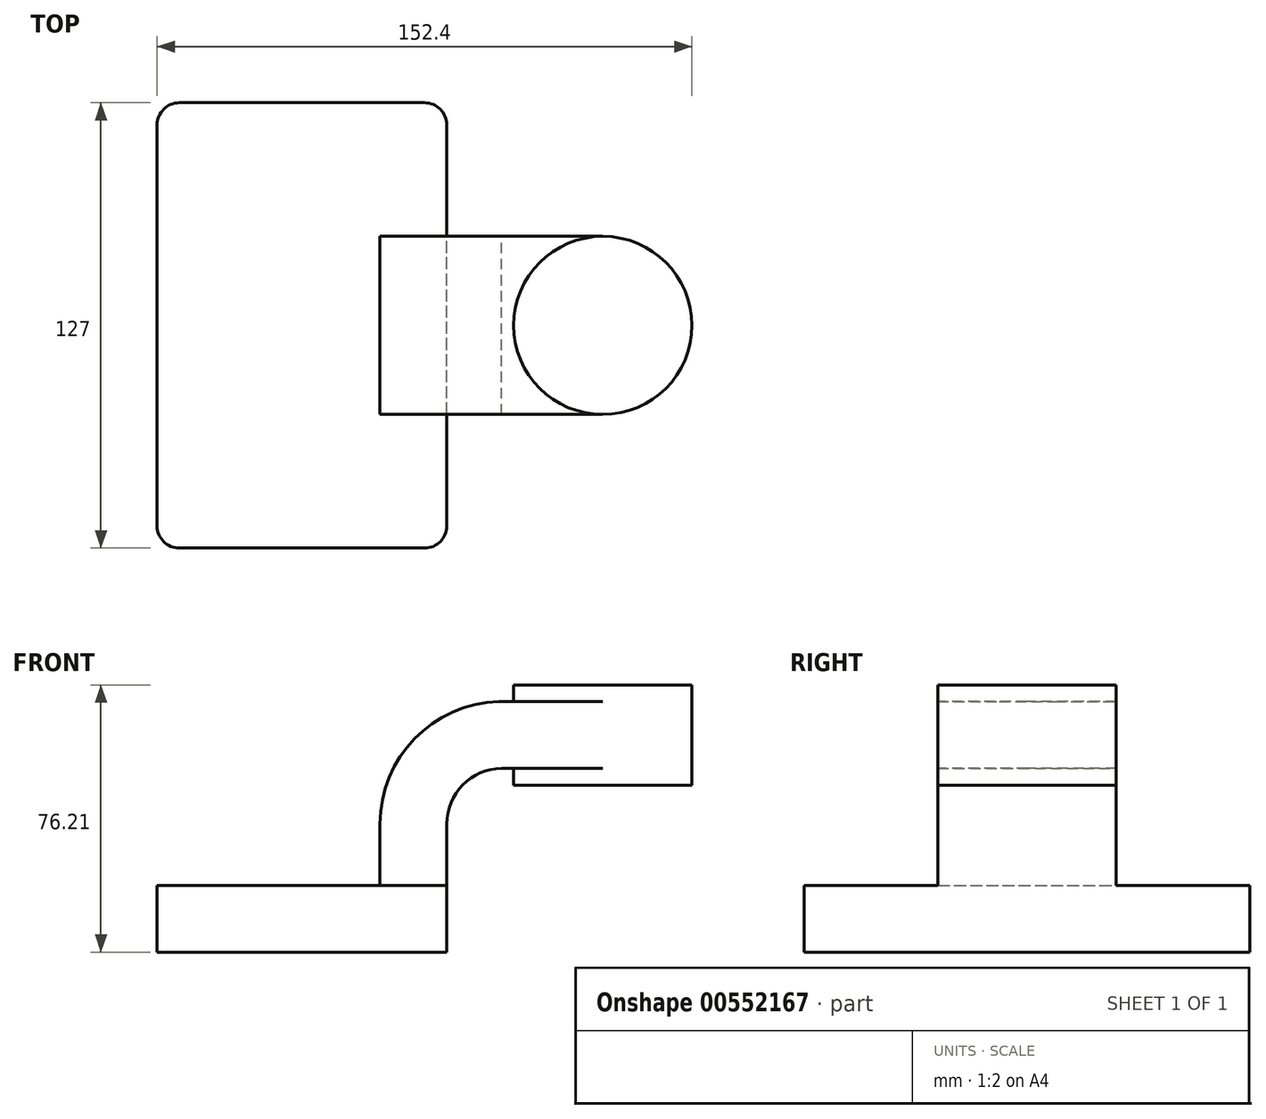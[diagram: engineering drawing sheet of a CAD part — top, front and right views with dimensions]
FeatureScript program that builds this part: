
annotation { "Feature Type Name" : "Feature", "Feature Type Description" : "" }
export const myFeature = defineFeature(function(context is Context, id is Id, definition is map)
    precondition{}
    {
        {
            var Q0;
            Q0=qCreatedBy(makeId("Front.planeOp"),FACE);
            var sketch = newSketch(context, id + "F0", { "sketchPlane" : qUnion([Q0])});
            skLineSegment(sketch, "E0.bottom", {"start": v(41.28, -9.52) * mm, "end": v(-41.28, -9.53) * mm});
            skLineSegment(sketch, "E0.top", {"start": v(41.28, 9.53) * mm, "end": v(-41.28, 9.53) * mm});
            skLineSegment(sketch, "E0.left", {"start": v(41.28, -9.52) * mm, "end": v(41.28, 9.53) * mm});
            skLineSegment(sketch, "E0.right", {"start": v(-41.28, -9.53) * mm, "end": v(-41.28, 9.53) * mm});
            skPoint(sketch, "E0.middle", {"position": v(0, 0) * mm});
            skLineSegment(sketch, "E1.bottom", {"start": v(111.12, 38.1) * mm, "end": v(60.32, 38.1) * mm});
            skLineSegment(sketch, "E1.top", {"start": v(111.12, 66.68) * mm, "end": v(60.32, 66.68) * mm});
            skLineSegment(sketch, "E1.left", {"start": v(111.12, 38.1) * mm, "end": v(111.12, 66.68) * mm});
            skLineSegment(sketch, "E1.right", {"start": v(60.32, 38.1) * mm, "end": v(60.32, 66.68) * mm});
            skPoint(sketch, "E1.middle", {"position": v(85.72, 52.39) * mm});
            skLineSegment(sketch, "E2", {"start": v(41.28, 9.53) * mm, "end": v(41.28, 27) * mm});
            skArc(sketch, "E3", {"start": v(41.27, 27) * mm, "mid": v(45.83, 38.13) * mm, "end": v(56.89, 42.88) * mm});
            skLineSegment(sketch, "E4", {"start": v(56.89, 42.88) * mm, "end": v(85.72, 42.88) * mm});
            skArc(sketch, "E5.0", {"start": v(22.23, 27) * mm, "mid": v(32.45, 51.7) * mm, "end": v(57.15, 61.93) * mm});
            skLineSegment(sketch, "E5.1", {"start": v(22.22, 9.53) * mm, "end": v(22.22, 27) * mm});
            skLineSegment(sketch, "E6", {"start": v(57.15, 61.93) * mm, "end": v(85.72, 61.93) * mm});
            skFitSpline(sketch, "E7", {"points": [v(-41.28, 9.52) * mm, v(57.15, 61.93) * mm], "startDerivative": vector(1.3, 63.2) * mm, "endDerivative": vector(133.3, 1.28) * mm});
            skLineSegment(sketch, "E8", {"start": v(85.72, 38.1) * mm, "end": v(85.72, 66.68) * mm});
            skSolve(sketch);
        }
        {
            var Q0;
            Q0=makeQuery(id+"F0.imprint","IMPRINT",FACE,{"disambiguationData":[TD([[makeQuery(id+"F0.imprint","IMPRINT",EDGE,{"derivedFrom":sQuery(id+"F0.wireOp",EDGE,"E0.bottom")}),-1.0]])]});
            extrude(context, id + "F1", {"entities" : qUnion([Q0]), "endBound" : BoundingType.SYMMETRIC, "depth" : 127 * mm, "offsetDistance" : 25.4 * mm});
        }
        {
            var Q0;
            {var subQ1=sQuery(id+"F0.wireOp",EDGE,"E2");Q0=makeQuery(id+"F0.imprint","IMPRINT",FACE,{"disambiguationData":[TD([[makeQuery(id+"F0.imprint","IMPRINT",EDGE,{"derivedFrom":subQ1}),1.0]])]});}
            var Q1;
            {var subQ0=sQuery(id+"F0.wireOp",EDGE,"E4");var subQ1=sQuery(id+"F0.wireOp",EDGE,"E1.right");var subQ2=makeQuery(id+"F0.imprint","INTERSECT",VERTEX,{"derivedFrom":[subQ1,subQ0]});Q1=makeQuery(id+"F0.imprint","IMPRINT",FACE,{"disambiguationData":[TD([[makeQuery(id+"F0.imprint","IMPRINT",EDGE,{"disambiguationData":[TD([[subQ2,-1.0]])],"derivedFrom":subQ1}),-1.0]])]});}
            extrude(context, id + "F2", {"entities" : qUnion([Q0, Q1]), "operationType" : NewBodyOperationType.ADD, "endBound" : BoundingType.SYMMETRIC, "depth" : 50.8 * mm, "offsetDistance" : 25.4 * mm});
        }
        {
            var Q0;
            Q0=makeQuery(id+"F0.imprint","IMPRINT",FACE,{"disambiguationData":[TD([[makeQuery(id+"F0.imprint","IMPRINT",EDGE,{"derivedFrom":sQuery(id+"F0.wireOp",EDGE,"E5.0")}),1.0]])]});
            extrude(context, id + "F3", {"entities" : qUnion([Q0]), "operationType" : NewBodyOperationType.ADD, "endBound" : BoundingType.SYMMETRIC, "depth" : 15.88 * mm, "offsetDistance" : 25.4 * mm});
        }
        {
            var Q0;
            {var subQ4=sQuery(id+"F0.wireOp",EDGE,"E1.left");Q0=makeQuery(id+"F0.imprint","IMPRINT",FACE,{"disambiguationData":[TD([[makeQuery(id+"F0.imprint","IMPRINT",EDGE,{"derivedFrom":subQ4}),1.0]])]});}
            var Q1;
            Q1=sQuery(id+"F0.wireOp",EDGE,"E8");
            revolve(context, id + "F4", {"operationType" : NewBodyOperationType.ADD, "entities" : qUnion([Q0]), "axis" : qUnion([Q1]), "revolveType" : RevolveType.FULL});
        }
        {
            var Q0;
            Q0=makeQuery(id+"F1.opExtrude","CAP_EDGE",EDGE,{"disambiguationData":[OSD([sQuery(id+"F0.wireOp",EDGE,"E0.left")])],"isStart":true});
            var Q1;
            Q1=makeQuery(id+"F1.opExtrude","CAP_EDGE",EDGE,{"disambiguationData":[OSD([sQuery(id+"F0.wireOp",EDGE,"E0.right")])],"isStart":true});
            var Q2;
            Q2=makeQuery(id+"F1.opExtrude","CAP_EDGE",EDGE,{"disambiguationData":[OSD([sQuery(id+"F0.wireOp",EDGE,"E0.right")])],"isStart":false});
            var Q3;
            Q3=makeQuery(id+"F1.opExtrude","CAP_EDGE",EDGE,{"disambiguationData":[OSD([sQuery(id+"F0.wireOp",EDGE,"E0.left")])],"isStart":false});
            fillet(context, id + "F5", {"entities" : qUnion([Q0, Q1, Q2, Q3]), "radius" : 6.35 * mm, "tangentPropagation" : true, "allowEdgeOverflow" : false});
        }
    });
